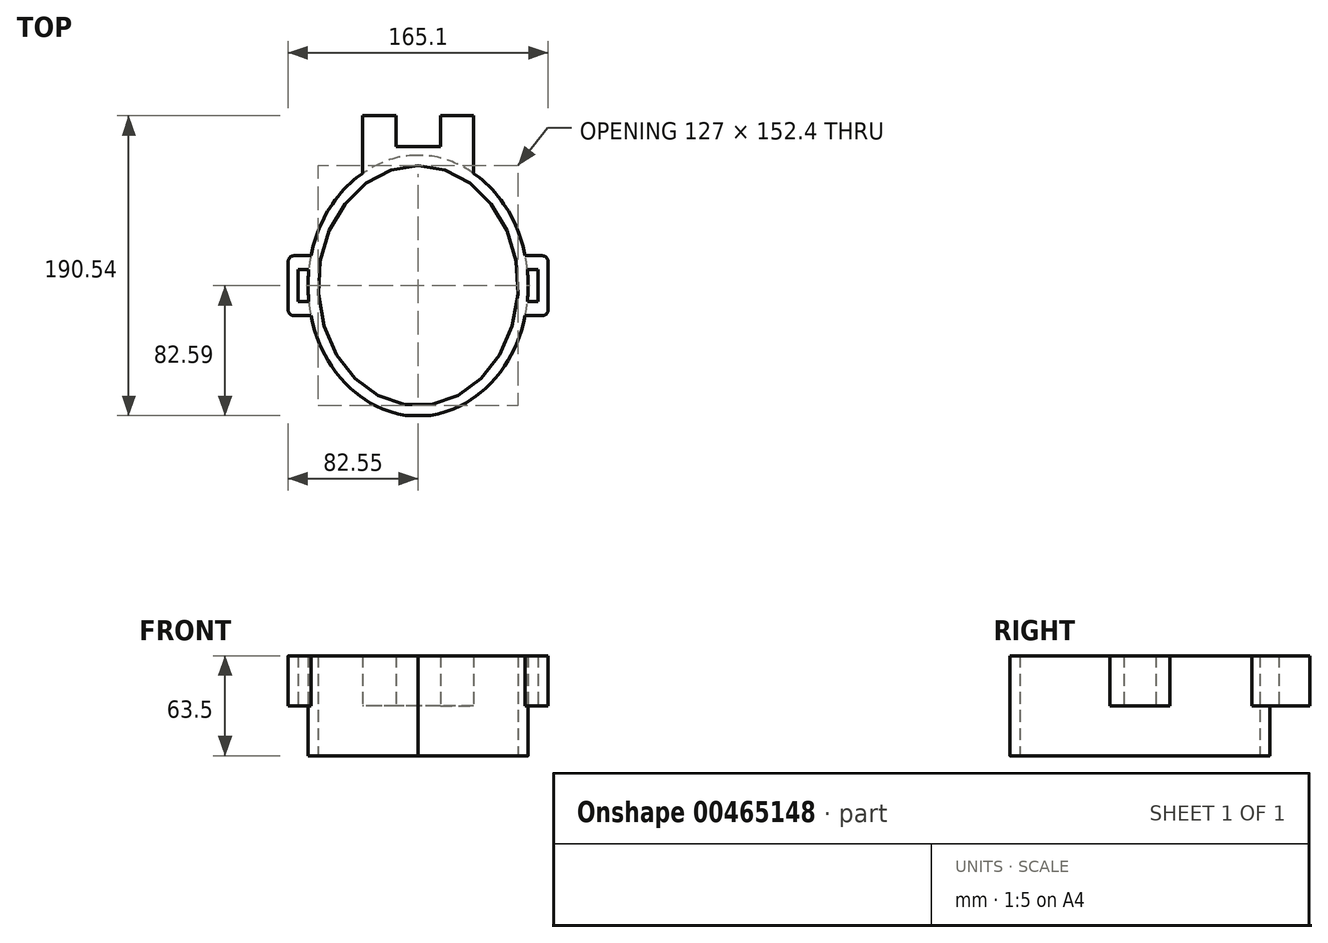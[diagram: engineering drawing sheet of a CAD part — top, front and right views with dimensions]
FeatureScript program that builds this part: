
annotation { "Feature Type Name" : "Feature", "Feature Type Description" : "" }
export const myFeature = defineFeature(function(context is Context, id is Id, definition is map)
    precondition{}
    {
        {
            var Q0;
            Q0=qCreatedBy(makeId("Top.planeOp"),FACE);
            var sketch = newSketch(context, id + "F0", { "sketchPlane" : qUnion([Q0])});
            skEllipticalArc(sketch, "E0", {});
            skPoint(sketch, "E1.startSnap0", {"position": v(0, -76.2) * mm});
            skLineSegment(sketch, "E2.right", {"start": v(-35.2, 107.95) * mm, "end": v(-35.2, 71.33) * mm});
            skPoint(sketch, "E2.middle", {"position": v(0, 95.25) * mm});
            skLineSegment(sketch, "E3.bottom", {"start": v(-67.97, 19.05) * mm, "end": v(-78.74, 19.05) * mm});
            skLineSegment(sketch, "E3.top", {"start": v(-67.97, -19.05) * mm, "end": v(-78.74, -19.05) * mm});
            skLineSegment(sketch, "E3.right", {"start": v(-82.55, 15.24) * mm, "end": v(-82.55, -15.24) * mm});
            skPoint(sketch, "E3.middle", {"position": v(-76.2, 0) * mm});
            skLineSegment(sketch, "E4", {"start": v(-76.2, 0) * mm, "end": v(-76.2, 10.16) * mm});
            skLineSegment(sketch, "E5", {"start": v(-76.2, 10.16) * mm, "end": v(-69.32, 10.16) * mm});
            skLineSegment(sketch, "E6", {"start": v(-76.2, 0) * mm, "end": v(-76.2, -10.16) * mm});
            skLineSegment(sketch, "E7", {"start": v(-76.2, -10.16) * mm, "end": v(-69.32, -10.16) * mm});
            skPoint(sketch, "E8.orphan", {"position": v(-69.85, 19.05) * mm});
            skPoint(sketch, "E9.orphan", {"position": v(-69.85, -19.05) * mm});
            skPoint(sketch, "E10.orphan", {"position": v(-69.85, 0) * mm});
            skPoint(sketch, "E11.end.orphan", {"position": v(-82.55, 0) * mm});
            skLineSegment(sketch, "E12.left", {"start": v(-14.13, 88.52) * mm, "end": v(-14.13, 107.95) * mm});
            skPoint(sketch, "E12.middle", {"position": v(0, 107.95) * mm});
            skPoint(sketch, "E13.orphan", {"position": v(-14.13, 127.38) * mm});
            skPoint(sketch, "E14.orphan", {"position": v(14.13, 127.38) * mm});
            skLineSegment(sketch, "E15.trimOffspring", {"start": v(-14.13, 107.95) * mm, "end": v(-35.2, 107.95) * mm});
            skPoint(sketch, "E16.orphan", {"position": v(35.2, 82.55) * mm});
            skPoint(sketch, "E2.top.end.orphan", {"position": v(-35.2, 82.55) * mm});
            skPoint(sketch, "E17.start.orphan", {"position": v(0, 82.55) * mm});
            skPoint(sketch, "E18.visualSharp", {"position": v(-82.55, 19.05) * mm});
            skArc(sketch, "E18.filletArc", {"start": v(-78.74, 19.05) * mm, "mid": v(-81.43, 17.93) * mm, "end": v(-82.55, 15.24) * mm});
            skPoint(sketch, "E19.visualSharp", {"position": v(-82.55, -19.05) * mm});
            skArc(sketch, "E19.filletArc", {"start": v(-82.55, -15.24) * mm, "mid": v(-81.43, -17.93) * mm, "end": v(-78.74, -19.05) * mm});
            skPoint(sketch, "E20.middle", {"position": v(0, -109.04) * mm});
            skPoint(sketch, "E21.middle", {"position": v(0, -82.55) * mm});
            skLineSegment(sketch, "E22", {"start": v(0, -111.15) * mm, "end": v(0, 206.62) * mm, "construction": true});
            skPoint(sketch, "E12.right.start.orphan", {"position": v(14.13, 88.52) * mm});
            skPoint(sketch, "E23.orphan", {"position": v(35.2, 107.95) * mm});
            skPoint(sketch, "E24.orphan", {"position": v(69.85, 0) * mm});
            skLineSegment(sketch, "E25", {"start": v(-14.13, 88.52) * mm, "end": v(0, 88.52) * mm});
            skLineSegment(sketch, "E26.MirrorCS", {"start": v(14.13, 88.52) * mm, "end": v(0, 88.52) * mm});
            skLineSegment(sketch, "E27.MirrorCS", {"start": v(14.13, 88.52) * mm, "end": v(14.13, 107.95) * mm});
            skLineSegment(sketch, "E28.MirrorCS", {"start": v(14.13, 107.95) * mm, "end": v(35.2, 107.95) * mm});
            skLineSegment(sketch, "E29.MirrorCS", {"start": v(35.2, 107.95) * mm, "end": v(35.2, 71.33) * mm});
            skEllipticalArc(sketch, "E30.MirrorCS", {});
            skLineSegment(sketch, "E31.MirrorCS", {"start": v(67.97, 19.05) * mm, "end": v(78.74, 19.05) * mm});
            skArc(sketch, "E32.MirrorCS", {"start": v(78.74, 19.05) * mm, "mid": v(81.43, 17.93) * mm, "end": v(82.55, 15.24) * mm});
            skLineSegment(sketch, "E33.MirrorCS", {"start": v(82.55, 15.24) * mm, "end": v(82.55, -15.24) * mm});
            skArc(sketch, "E34.MirrorCS", {"start": v(82.55, -15.24) * mm, "mid": v(81.43, -17.93) * mm, "end": v(78.74, -19.05) * mm});
            skLineSegment(sketch, "E35.MirrorCS", {"start": v(67.97, -19.05) * mm, "end": v(78.74, -19.05) * mm});
            skLineSegment(sketch, "E36.MirrorCS", {"start": v(76.2, -10.16) * mm, "end": v(69.32, -10.16) * mm});
            skLineSegment(sketch, "E37.MirrorCS", {"start": v(76.2, 0) * mm, "end": v(76.2, -10.16) * mm});
            skLineSegment(sketch, "E38.MirrorCS", {"start": v(76.2, 0) * mm, "end": v(76.2, 10.16) * mm});
            skLineSegment(sketch, "E39.MirrorCS", {"start": v(76.2, 10.16) * mm, "end": v(69.32, 10.16) * mm});
            skFitSpline(sketch, "E40.0", {"points": [v(0, -82.55) * mm, v(4.68, -82.55) * mm, v(11.66, -81.72) * mm, v(20.63, -79.02) * mm, v(27.15, -76.22) * mm, v(32.36, -73.27) * mm, v(36.38, -70.54) * mm, v(40.25, -67.6) * mm, v(44.83, -63.51) * mm, v(49.86, -58.04) * mm, v(54.4, -52.02) * mm, v(57.76, -46.6) * mm, v(60.17, -42.04) * mm, v(62.39, -37.33) * mm, v(64.78, -31.26) * mm, v(67.03, -23.7) * mm, v(68.65, -15.94) * mm, v(69.47, -9.35) * mm, v(69.8, -4.02) * mm, v(69.88, 0) * mm, v(69.8, 4.02) * mm, v(69.47, 9.35) * mm, v(68.65, 15.94) * mm, v(67.03, 23.7) * mm, v(64.78, 31.26) * mm, v(62.39, 37.33) * mm, v(60.17, 42.04) * mm, v(57.76, 46.6) * mm, v(54.4, 52.02) * mm, v(49.86, 58.04) * mm, v(44.83, 63.51) * mm, v(40.25, 67.6) * mm, v(36.38, 70.54) * mm, v(32.36, 73.27) * mm, v(27.15, 76.22) * mm, v(20.63, 79.02) * mm, v(11.66, 81.72) * mm, v(4.68, 82.55) * mm, v(0, 82.55) * mm]});
            skFitSpline(sketch, "E40.1", {"points": [v(0, 82.55) * mm, v(-4.68, 82.55) * mm, v(-11.66, 81.72) * mm, v(-20.63, 79.02) * mm, v(-27.15, 76.22) * mm, v(-32.36, 73.27) * mm, v(-36.38, 70.54) * mm, v(-40.25, 67.6) * mm, v(-44.83, 63.51) * mm, v(-49.86, 58.04) * mm, v(-54.4, 52.02) * mm, v(-57.76, 46.6) * mm, v(-60.17, 42.04) * mm, v(-62.39, 37.33) * mm, v(-64.78, 31.26) * mm, v(-67.03, 23.7) * mm, v(-68.65, 15.94) * mm, v(-69.47, 9.35) * mm, v(-69.8, 4.02) * mm, v(-69.88, 0) * mm, v(-69.8, -4.02) * mm, v(-69.47, -9.35) * mm, v(-68.65, -15.94) * mm, v(-67.03, -23.7) * mm, v(-64.78, -31.26) * mm, v(-62.39, -37.33) * mm, v(-60.17, -42.04) * mm, v(-57.76, -46.6) * mm, v(-54.4, -52.02) * mm, v(-49.86, -58.04) * mm, v(-44.83, -63.51) * mm, v(-40.25, -67.6) * mm, v(-36.38, -70.54) * mm, v(-32.36, -73.27) * mm, v(-27.15, -76.22) * mm, v(-20.63, -79.02) * mm, v(-11.66, -81.72) * mm, v(-4.68, -82.55) * mm, v(0, -82.55) * mm]});
            skFitSpline(sketch, "E41.0", {"points": [v(0, -82.55) * mm, v(4.68, -82.55) * mm, v(11.66, -81.72) * mm, v(20.63, -79.02) * mm, v(27.15, -76.22) * mm, v(32.36, -73.27) * mm, v(36.38, -70.54) * mm, v(40.25, -67.6) * mm, v(44.83, -63.51) * mm, v(49.86, -58.04) * mm, v(54.4, -52.02) * mm, v(57.76, -46.6) * mm, v(60.17, -42.04) * mm, v(62.39, -37.33) * mm, v(64.78, -31.26) * mm, v(67.03, -23.7) * mm, v(68.65, -15.94) * mm, v(69.47, -9.35) * mm, v(69.8, -4.02) * mm, v(69.88, 0) * mm, v(69.8, 4.02) * mm, v(69.47, 9.35) * mm, v(68.65, 15.94) * mm, v(67.03, 23.7) * mm, v(64.78, 31.26) * mm, v(62.39, 37.33) * mm, v(60.17, 42.04) * mm, v(57.76, 46.6) * mm, v(54.4, 52.02) * mm, v(49.86, 58.04) * mm, v(44.83, 63.51) * mm, v(40.25, 67.6) * mm, v(36.38, 70.54) * mm, v(32.36, 73.27) * mm, v(27.15, 76.22) * mm, v(20.63, 79.02) * mm, v(11.66, 81.72) * mm, v(4.68, 82.55) * mm, v(0, 82.55) * mm]});
            const initialGuessF0  = {"E0": [0, 0, 0, 1, 0.0762, 0.0635, 0, 3.141592653589793], "E30.MirrorCS": [0, 0, 0, 1, 0.0762, 0.0635, 3.141592653589793, 0]};
            skSetInitialGuess(sketch, initialGuessF0);
            skSolve(sketch);
        }
        {
            var Q0;
            Q0=makeQuery(id+"F0.imprint","IMPRINT",FACE,{"disambiguationData":[TD([[makeQuery(id+"F0.imprint","IMPRINT",EDGE,{"derivedFrom":sQuery(id+"F0.wireOp",EDGE,"E0")}),-1.0]])]});
            extrude(context, id + "F1", {"entities" : qUnion([Q0]), "endBound" : BoundingType.SYMMETRIC, "depth" : 63.5 * mm});
        }
        {
            var Q0;
            Q0 = qSketchRegion(id + "F0", true);
            var Q1;
            Q1=makeQuery(id+"F1.opExtrude","CAP_FACE",FACE,{"disambiguationData":[OSD([sQuery(id+"F0.wireOp",EDGE,"E0"),sQuery(id+"F0.wireOp",EDGE,"E30.MirrorCS"),sQuery(id+"F0.wireOp",EDGE,"E40.1"),sQuery(id+"F0.wireOp",EDGE,"E41.0")])],"isStart":false});
            extrude(context, id + "F2", {"entities" : qUnion([Q0]), "operationType" : NewBodyOperationType.ADD, "endBound" : BoundingType.UP_TO_SURFACE, "endBoundEntityFace" : qUnion([Q1]), "depth" : 25.4 * mm});
        }
    });
